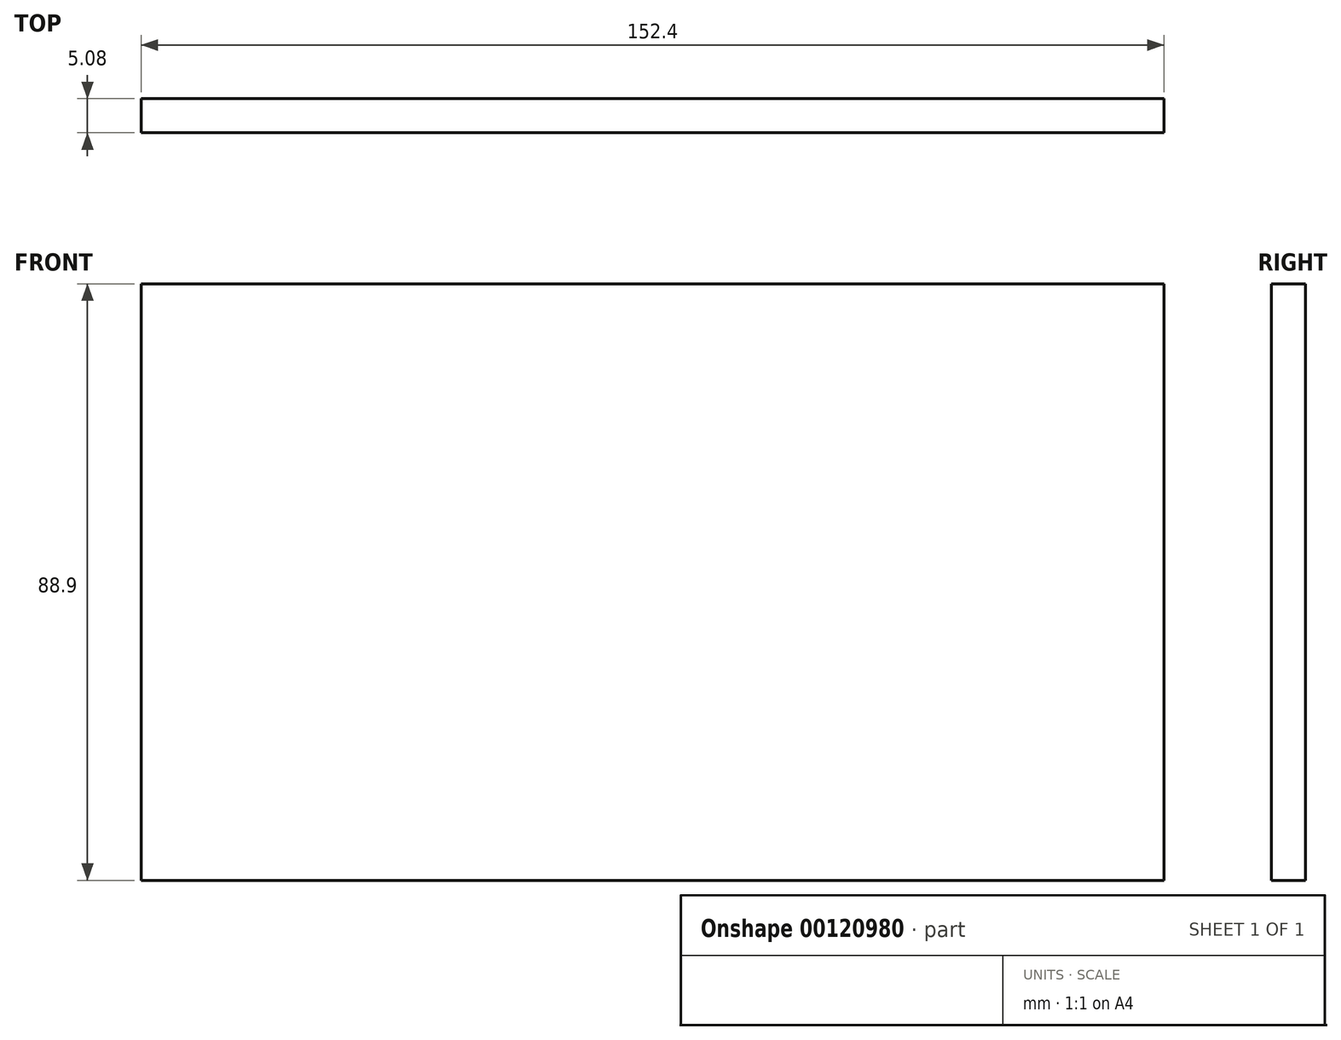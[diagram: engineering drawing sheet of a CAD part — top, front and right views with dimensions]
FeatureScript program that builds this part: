
annotation { "Feature Type Name" : "Feature", "Feature Type Description" : "" }
export const myFeature = defineFeature(function(context is Context, id is Id, definition is map)
    precondition{}
    {
        {
            var Q0;
            Q0=qCreatedBy(makeId("Front.planeOp"),FACE);
            var sketch = newSketch(context, id + "F0", { "sketchPlane" : qUnion([Q0])});
            skLineSegment(sketch, "E0.bottom", {"start": v(-110.02, 20.94) * mm, "end": v(42.38, 20.94) * mm});
            skLineSegment(sketch, "E0.top", {"start": v(-110.02, -67.96) * mm, "end": v(42.38, -67.96) * mm});
            skLineSegment(sketch, "E0.right", {"start": v(42.38, 20.94) * mm, "end": v(42.38, -67.96) * mm});
            skLineSegment(sketch, "E1", {"start": v(-110.02, 20.94) * mm, "end": v(-110.02, -67.96) * mm});
            skSolve(sketch);
        }
        {
            var Q0;
            Q0=qSketchRegion(id+"F0",true);
            extrude(context, id + "F1", {"entities" : qUnion([Q0]), "oppositeDirection" : true, "depth" : 5.08 * mm});
        }
    });
